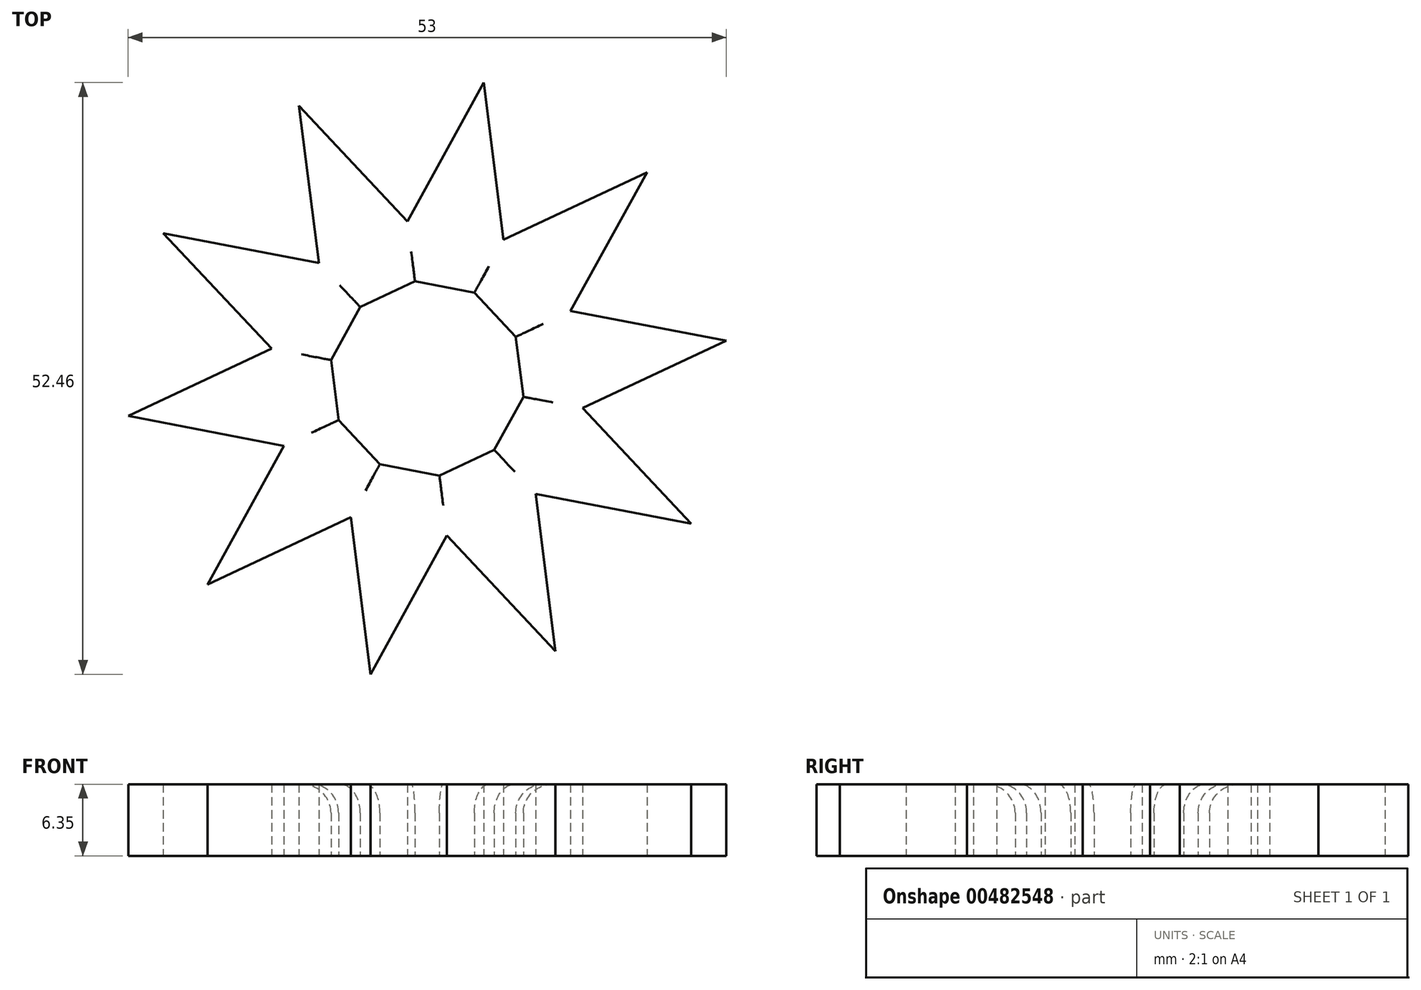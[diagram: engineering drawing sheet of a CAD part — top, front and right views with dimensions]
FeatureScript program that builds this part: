
annotation { "Feature Type Name" : "Feature", "Feature Type Description" : "" }
export const myFeature = defineFeature(function(context is Context, id is Id, definition is map)
    precondition{}
    {
        {
            var Q0;
            Q0=qCreatedBy(makeId("Top.planeOp"),FACE);
            var sketch = newSketch(context, id + "F0", { "sketchPlane" : qUnion([Q0])});
            skCircle(sketch, "E0.cCircle", {"center": v(0, 0) * mm, "radius": 25.4 * mm, "construction": true});
            skLineSegment(sketch, "E0.0", {"start": v(-23.4, 12.88) * mm, "end": v(-11.36, 24.17) * mm});
            skLineSegment(sketch, "E0.1", {"start": v(-11.36, 24.17) * mm, "end": v(5.02, 26.23) * mm});
            skLineSegment(sketch, "E0.2", {"start": v(5.02, 26.23) * mm, "end": v(19.48, 18.27) * mm});
            skLineSegment(sketch, "E0.3", {"start": v(19.48, 18.27) * mm, "end": v(26.5, 3.34) * mm});
            skLineSegment(sketch, "E0.4", {"start": v(26.5, 3.34) * mm, "end": v(23.4, -12.88) * mm});
            skLineSegment(sketch, "E0.5", {"start": v(23.4, -12.88) * mm, "end": v(11.36, -24.17) * mm});
            skLineSegment(sketch, "E0.6", {"start": v(11.36, -24.17) * mm, "end": v(-5.02, -26.23) * mm});
            skLineSegment(sketch, "E0.7", {"start": v(-5.02, -26.23) * mm, "end": v(-19.48, -18.27) * mm});
            skLineSegment(sketch, "E0.8", {"start": v(-19.48, -18.27) * mm, "end": v(-26.5, -3.34) * mm});
            skLineSegment(sketch, "E0.9", {"start": v(-26.5, -3.34) * mm, "end": v(-23.4, 12.88) * mm});
            skPoint(sketch, "E0.0.midPoint", {"position": v(-17.38, 18.52) * mm});
            skLineSegment(sketch, "E1", {"start": v(-19.48, -18.27) * mm, "end": v(5.02, 26.23) * mm});
            skLineSegment(sketch, "E2", {"start": v(5.02, 26.23) * mm, "end": v(11.36, -24.17) * mm});
            skLineSegment(sketch, "E3", {"start": v(11.36, -24.17) * mm, "end": v(-23.4, 12.88) * mm});
            skLineSegment(sketch, "E4", {"start": v(-23.4, 12.88) * mm, "end": v(26.5, 3.34) * mm});
            skLineSegment(sketch, "E5", {"start": v(26.5, 3.34) * mm, "end": v(-19.48, -18.27) * mm});
            skLineSegment(sketch, "E6", {"start": v(-26.5, -3.34) * mm, "end": v(19.48, 18.27) * mm});
            skLineSegment(sketch, "E7", {"start": v(19.48, 18.27) * mm, "end": v(-5.02, -26.23) * mm});
            skLineSegment(sketch, "E8", {"start": v(-5.02, -26.23) * mm, "end": v(-11.36, 24.17) * mm});
            skLineSegment(sketch, "E9", {"start": v(-11.36, 24.17) * mm, "end": v(23.4, -12.88) * mm});
            skLineSegment(sketch, "E10", {"start": v(23.4, -12.88) * mm, "end": v(-26.5, -3.34) * mm});
            skSolve(sketch);
        }
        {
            var Q0;
            {var subQ1=sQuery(id+"F0.wireOp",EDGE,"E3");var subQ3=sQuery(id+"F0.wireOp",EDGE,"E6");var subQ4=makeQuery(id+"F0.imprint","INTERSECT",VERTEX,{"derivedFrom":[subQ1,subQ3]});Q0=makeQuery(id+"F0.imprint","IMPRINT",FACE,{"disambiguationData":[TD([[makeQuery(id+"F0.imprint","IMPRINT",EDGE,{"disambiguationData":[TD([[subQ4,-1.0]])],"derivedFrom":subQ3}),1.0]])]});}
            var Q1;
            {var subQ0=sQuery(id+"F0.wireOp",EDGE,"E3");var subQ1=sQuery(id+"F0.wireOp",EDGE,"E1");var subQ2=makeQuery(id+"F0.imprint","INTERSECT",VERTEX,{"derivedFrom":[subQ1,subQ0]});Q1=makeQuery(id+"F0.imprint","IMPRINT",FACE,{"disambiguationData":[TD([[makeQuery(id+"F0.imprint","IMPRINT",EDGE,{"disambiguationData":[TD([[subQ2,-1.0]])],"derivedFrom":subQ1}),1.0]])]});}
            var Q2;
            {var subQ0=sQuery(id+"F0.wireOp",EDGE,"E10");var subQ1=sQuery(id+"F0.wireOp",EDGE,"E1");var subQ2=makeQuery(id+"F0.imprint","INTERSECT",VERTEX,{"derivedFrom":[subQ1,subQ0]});Q2=makeQuery(id+"F0.imprint","IMPRINT",FACE,{"disambiguationData":[TD([[makeQuery(id+"F0.imprint","IMPRINT",EDGE,{"disambiguationData":[TD([[subQ2,-1.0]])],"derivedFrom":subQ1}),1.0]])]});}
            var Q3;
            {var subQ0=sQuery(id+"F0.wireOp",EDGE,"E5");var subQ5=sQuery(id+"F0.wireOp",EDGE,"E8");var subQ6=makeQuery(id+"F0.imprint","INTERSECT",VERTEX,{"derivedFrom":[subQ0,subQ5]});Q3=makeQuery(id+"F0.imprint","IMPRINT",FACE,{"disambiguationData":[TD([[makeQuery(id+"F0.imprint","IMPRINT",EDGE,{"disambiguationData":[TD([[subQ6,-1.0]])],"derivedFrom":subQ5}),1.0]])]});}
            var Q4;
            {var subQ0=sQuery(id+"F0.wireOp",EDGE,"E7");var subQ1=sQuery(id+"F0.wireOp",EDGE,"E3");var subQ2=makeQuery(id+"F0.imprint","INTERSECT",VERTEX,{"derivedFrom":[subQ1,subQ0]});Q4=makeQuery(id+"F0.imprint","IMPRINT",FACE,{"disambiguationData":[TD([[makeQuery(id+"F0.imprint","IMPRINT",EDGE,{"disambiguationData":[TD([[subQ2,-1.0]])],"derivedFrom":subQ1}),1.0]])]});}
            var Q5;
            {var subQ0=sQuery(id+"F0.wireOp",EDGE,"E3");var subQ5=sQuery(id+"F0.wireOp",EDGE,"E7");var subQ6=makeQuery(id+"F0.imprint","INTERSECT",VERTEX,{"derivedFrom":[subQ0,subQ5]});Q5=makeQuery(id+"F0.imprint","IMPRINT",FACE,{"disambiguationData":[TD([[makeQuery(id+"F0.imprint","IMPRINT",EDGE,{"disambiguationData":[TD([[subQ6,1.0]])],"derivedFrom":subQ5}),1.0]])]});}
            var Q6;
            {var subQ0=sQuery(id+"F0.wireOp",EDGE,"E5");var subQ1=sQuery(id+"F0.wireOp",EDGE,"E2");var subQ2=makeQuery(id+"F0.imprint","INTERSECT",VERTEX,{"derivedFrom":[subQ1,subQ0]});Q6=makeQuery(id+"F0.imprint","IMPRINT",FACE,{"disambiguationData":[TD([[makeQuery(id+"F0.imprint","IMPRINT",EDGE,{"disambiguationData":[TD([[subQ2,-1.0]])],"derivedFrom":subQ1}),1.0]])]});}
            var Q7;
            {var subQ1=sQuery(id+"F0.wireOp",EDGE,"E4");var subQ3=sQuery(id+"F0.wireOp",EDGE,"E7");var subQ4=makeQuery(id+"F0.imprint","INTERSECT",VERTEX,{"derivedFrom":[subQ1,subQ3]});Q7=makeQuery(id+"F0.imprint","IMPRINT",FACE,{"disambiguationData":[TD([[makeQuery(id+"F0.imprint","IMPRINT",EDGE,{"disambiguationData":[TD([[subQ4,-1.0]])],"derivedFrom":subQ3}),1.0]])]});}
            var Q8;
            {var subQ0=sQuery(id+"F0.wireOp",EDGE,"E6");var subQ1=sQuery(id+"F0.wireOp",EDGE,"E2");var subQ2=makeQuery(id+"F0.imprint","INTERSECT",VERTEX,{"derivedFrom":[subQ1,subQ0]});Q8=makeQuery(id+"F0.imprint","IMPRINT",FACE,{"disambiguationData":[TD([[makeQuery(id+"F0.imprint","IMPRINT",EDGE,{"disambiguationData":[TD([[subQ2,-1.0]])],"derivedFrom":subQ1}),1.0]])]});}
            var Q9;
            {var subQ0=sQuery(id+"F0.wireOp",EDGE,"E2");var subQ5=sQuery(id+"F0.wireOp",EDGE,"E6");var subQ6=makeQuery(id+"F0.imprint","INTERSECT",VERTEX,{"derivedFrom":[subQ0,subQ5]});Q9=makeQuery(id+"F0.imprint","IMPRINT",FACE,{"disambiguationData":[TD([[makeQuery(id+"F0.imprint","IMPRINT",EDGE,{"disambiguationData":[TD([[subQ6,1.0]])],"derivedFrom":subQ5}),1.0]])]});}
            var Q10;
            {var subQ0=sQuery(id+"F0.wireOp",EDGE,"E4");var subQ1=sQuery(id+"F0.wireOp",EDGE,"E1");var subQ2=makeQuery(id+"F0.imprint","INTERSECT",VERTEX,{"derivedFrom":[subQ1,subQ0]});Q10=makeQuery(id+"F0.imprint","IMPRINT",FACE,{"disambiguationData":[TD([[makeQuery(id+"F0.imprint","IMPRINT",EDGE,{"disambiguationData":[TD([[subQ2,-1.0]])],"derivedFrom":subQ1}),1.0]])]});}
            var Q11;
            {var subQ0=sQuery(id+"F0.wireOp",EDGE,"E6");var subQ1=sQuery(id+"F0.wireOp",EDGE,"E1");var subQ2=makeQuery(id+"F0.imprint","INTERSECT",VERTEX,{"derivedFrom":[subQ1,subQ0]});Q11=makeQuery(id+"F0.imprint","IMPRINT",FACE,{"disambiguationData":[TD([[makeQuery(id+"F0.imprint","IMPRINT",EDGE,{"disambiguationData":[TD([[subQ2,-1.0]])],"derivedFrom":subQ1}),1.0]])]});}
            var Q12;
            {var subQ0=sQuery(id+"F0.wireOp",EDGE,"E4");var subQ1=sQuery(id+"F0.wireOp",EDGE,"E1");var subQ2=makeQuery(id+"F0.imprint","INTERSECT",VERTEX,{"derivedFrom":[subQ1,subQ0]});Q12=makeQuery(id+"F0.imprint","IMPRINT",FACE,{"disambiguationData":[TD([[makeQuery(id+"F0.imprint","IMPRINT",EDGE,{"disambiguationData":[TD([[subQ2,-1.0]])],"derivedFrom":subQ1}),-1.0]])]});}
            var Q13;
            {var subQ0=sQuery(id+"F0.wireOp",EDGE,"E6");var subQ1=sQuery(id+"F0.wireOp",EDGE,"E2");var subQ2=makeQuery(id+"F0.imprint","INTERSECT",VERTEX,{"derivedFrom":[subQ1,subQ0]});Q13=makeQuery(id+"F0.imprint","IMPRINT",FACE,{"disambiguationData":[TD([[makeQuery(id+"F0.imprint","IMPRINT",EDGE,{"disambiguationData":[TD([[subQ2,-1.0]])],"derivedFrom":subQ1}),-1.0]])]});}
            var Q14;
            {var subQ0=sQuery(id+"F0.wireOp",EDGE,"E4");var subQ1=sQuery(id+"F0.wireOp",EDGE,"E2");var subQ2=makeQuery(id+"F0.imprint","INTERSECT",VERTEX,{"derivedFrom":[subQ1,subQ0]});Q14=makeQuery(id+"F0.imprint","IMPRINT",FACE,{"disambiguationData":[TD([[makeQuery(id+"F0.imprint","IMPRINT",EDGE,{"disambiguationData":[TD([[subQ2,-1.0]])],"derivedFrom":subQ1}),1.0]])]});}
            var Q15;
            {var subQ0=sQuery(id+"F0.wireOp",EDGE,"E5");var subQ1=sQuery(id+"F0.wireOp",EDGE,"E2");var subQ2=makeQuery(id+"F0.imprint","INTERSECT",VERTEX,{"derivedFrom":[subQ1,subQ0]});Q15=makeQuery(id+"F0.imprint","IMPRINT",FACE,{"disambiguationData":[TD([[makeQuery(id+"F0.imprint","IMPRINT",EDGE,{"disambiguationData":[TD([[subQ2,-1.0]])],"derivedFrom":subQ1}),-1.0]])]});}
            var Q16;
            {var subQ0=sQuery(id+"F0.wireOp",EDGE,"E7");var subQ1=sQuery(id+"F0.wireOp",EDGE,"E3");var subQ2=makeQuery(id+"F0.imprint","INTERSECT",VERTEX,{"derivedFrom":[subQ1,subQ0]});Q16=makeQuery(id+"F0.imprint","IMPRINT",FACE,{"disambiguationData":[TD([[makeQuery(id+"F0.imprint","IMPRINT",EDGE,{"disambiguationData":[TD([[subQ2,-1.0]])],"derivedFrom":subQ1}),-1.0]])]});}
            var Q17;
            {var subQ0=sQuery(id+"F0.wireOp",EDGE,"E5");var subQ1=sQuery(id+"F0.wireOp",EDGE,"E3");var subQ2=makeQuery(id+"F0.imprint","INTERSECT",VERTEX,{"derivedFrom":[subQ1,subQ0]});Q17=makeQuery(id+"F0.imprint","IMPRINT",FACE,{"disambiguationData":[TD([[makeQuery(id+"F0.imprint","IMPRINT",EDGE,{"disambiguationData":[TD([[subQ2,-1.0]])],"derivedFrom":subQ1}),1.0]])]});}
            var Q18;
            {var subQ0=sQuery(id+"F0.wireOp",EDGE,"E10");var subQ1=sQuery(id+"F0.wireOp",EDGE,"E1");var subQ2=makeQuery(id+"F0.imprint","INTERSECT",VERTEX,{"derivedFrom":[subQ1,subQ0]});Q18=makeQuery(id+"F0.imprint","IMPRINT",FACE,{"disambiguationData":[TD([[makeQuery(id+"F0.imprint","IMPRINT",EDGE,{"disambiguationData":[TD([[subQ2,-1.0]])],"derivedFrom":subQ1}),-1.0]])]});}
            var Q19;
            {var subQ0=sQuery(id+"F0.wireOp",EDGE,"E5");var subQ1=sQuery(id+"F0.wireOp",EDGE,"E3");var subQ2=makeQuery(id+"F0.imprint","INTERSECT",VERTEX,{"derivedFrom":[subQ1,subQ0]});Q19=makeQuery(id+"F0.imprint","IMPRINT",FACE,{"disambiguationData":[TD([[makeQuery(id+"F0.imprint","IMPRINT",EDGE,{"disambiguationData":[TD([[subQ2,-1.0]])],"derivedFrom":subQ1}),-1.0]])]});}
            var Q20;
            {var subQ0=sQuery(id+"F0.wireOp",EDGE,"E7");var subQ1=sQuery(id+"F0.wireOp",EDGE,"E5");var subQ2=makeQuery(id+"F0.imprint","INTERSECT",VERTEX,{"derivedFrom":[subQ1,subQ0]});Q20=makeQuery(id+"F0.imprint","IMPRINT",FACE,{"disambiguationData":[TD([[makeQuery(id+"F0.imprint","IMPRINT",EDGE,{"disambiguationData":[TD([[subQ2,-1.0]])],"derivedFrom":subQ1}),1.0]])]});}
            var Q21;
            {var subQ0=sQuery(id+"F0.wireOp",EDGE,"E7");var subQ1=sQuery(id+"F0.wireOp",EDGE,"E2");var subQ2=makeQuery(id+"F0.imprint","INTERSECT",VERTEX,{"derivedFrom":[subQ1,subQ0]});Q21=makeQuery(id+"F0.imprint","IMPRINT",FACE,{"disambiguationData":[TD([[makeQuery(id+"F0.imprint","IMPRINT",EDGE,{"disambiguationData":[TD([[subQ2,-1.0]])],"derivedFrom":subQ1}),-1.0]])]});}
            var Q22;
            {var subQ0=sQuery(id+"F0.wireOp",EDGE,"E4");var subQ1=sQuery(id+"F0.wireOp",EDGE,"E2");var subQ2=makeQuery(id+"F0.imprint","INTERSECT",VERTEX,{"derivedFrom":[subQ1,subQ0]});Q22=makeQuery(id+"F0.imprint","IMPRINT",FACE,{"disambiguationData":[TD([[makeQuery(id+"F0.imprint","IMPRINT",EDGE,{"disambiguationData":[TD([[subQ2,-1.0]])],"derivedFrom":subQ1}),-1.0]])]});}
            var Q23;
            {var subQ0=sQuery(id+"F0.wireOp",EDGE,"E7");var subQ1=sQuery(id+"F0.wireOp",EDGE,"E2");var subQ2=makeQuery(id+"F0.imprint","INTERSECT",VERTEX,{"derivedFrom":[subQ1,subQ0]});Q23=makeQuery(id+"F0.imprint","IMPRINT",FACE,{"disambiguationData":[TD([[makeQuery(id+"F0.imprint","IMPRINT",EDGE,{"disambiguationData":[TD([[subQ2,-1.0]])],"derivedFrom":subQ1}),1.0]])]});}
            var Q24;
            {var subQ0=sQuery(id+"F0.wireOp",EDGE,"E9");var subQ1=sQuery(id+"F0.wireOp",EDGE,"E2");var subQ2=makeQuery(id+"F0.imprint","INTERSECT",VERTEX,{"derivedFrom":[subQ1,subQ0]});Q24=makeQuery(id+"F0.imprint","IMPRINT",FACE,{"disambiguationData":[TD([[makeQuery(id+"F0.imprint","IMPRINT",EDGE,{"disambiguationData":[TD([[subQ2,-1.0]])],"derivedFrom":subQ1}),1.0]])]});}
            var Q25;
            {var subQ0=sQuery(id+"F0.wireOp",EDGE,"E6");var subQ1=sQuery(id+"F0.wireOp",EDGE,"E4");var subQ2=makeQuery(id+"F0.imprint","INTERSECT",VERTEX,{"derivedFrom":[subQ1,subQ0]});Q25=makeQuery(id+"F0.imprint","IMPRINT",FACE,{"disambiguationData":[TD([[makeQuery(id+"F0.imprint","IMPRINT",EDGE,{"disambiguationData":[TD([[subQ2,-1.0]])],"derivedFrom":subQ1}),1.0]])]});}
            var Q26;
            {var subQ0=sQuery(id+"F0.wireOp",EDGE,"E6");var subQ1=sQuery(id+"F0.wireOp",EDGE,"E1");var subQ2=makeQuery(id+"F0.imprint","INTERSECT",VERTEX,{"derivedFrom":[subQ1,subQ0]});Q26=makeQuery(id+"F0.imprint","IMPRINT",FACE,{"disambiguationData":[TD([[makeQuery(id+"F0.imprint","IMPRINT",EDGE,{"disambiguationData":[TD([[subQ2,-1.0]])],"derivedFrom":subQ1}),-1.0]])]});}
            var Q27;
            {var subQ0=sQuery(id+"F0.wireOp",EDGE,"E3");var subQ1=sQuery(id+"F0.wireOp",EDGE,"E1");var subQ2=makeQuery(id+"F0.imprint","INTERSECT",VERTEX,{"derivedFrom":[subQ1,subQ0]});Q27=makeQuery(id+"F0.imprint","IMPRINT",FACE,{"disambiguationData":[TD([[makeQuery(id+"F0.imprint","IMPRINT",EDGE,{"disambiguationData":[TD([[subQ2,-1.0]])],"derivedFrom":subQ1}),-1.0]])]});}
            var Q28;
            {var subQ0=sQuery(id+"F0.wireOp",EDGE,"E10");var subQ1=sQuery(id+"F0.wireOp",EDGE,"E3");var subQ2=makeQuery(id+"F0.imprint","INTERSECT",VERTEX,{"derivedFrom":[subQ1,subQ0]});Q28=makeQuery(id+"F0.imprint","IMPRINT",FACE,{"disambiguationData":[TD([[makeQuery(id+"F0.imprint","IMPRINT",EDGE,{"disambiguationData":[TD([[subQ2,-1.0]])],"derivedFrom":subQ1}),1.0]])]});}
            var Q29;
            {var subQ0=sQuery(id+"F0.wireOp",EDGE,"E8");var subQ1=sQuery(id+"F0.wireOp",EDGE,"E1");var subQ2=makeQuery(id+"F0.imprint","INTERSECT",VERTEX,{"derivedFrom":[subQ1,subQ0]});Q29=makeQuery(id+"F0.imprint","IMPRINT",FACE,{"disambiguationData":[TD([[makeQuery(id+"F0.imprint","IMPRINT",EDGE,{"disambiguationData":[TD([[subQ2,-1.0]])],"derivedFrom":subQ1}),1.0]])]});}
            extrude(context, id + "F1", {"entities" : qUnion([Q0, Q1, Q2, Q3, Q4, Q5, Q6, Q7, Q8, Q9, Q10, Q11, Q12, Q13, Q14, Q15, Q16, Q17, Q18, Q19, Q20, Q21, Q22, Q23, Q24, Q25, Q26, Q27, Q28, Q29]), "depth" : 6.35 * mm});
        }
        {
            var Q0;
            {var subQ0=sQuery(id+"F0.wireOp",EDGE,"E9");Q0=makeQuery(id+"F1.opExtrude","CAP_EDGE",EDGE,{"disambiguationData":[OSD([subQ0]),TDD([makeQuery(id+"F0.imprint","IMPRINT",EDGE,{"disambiguationData":[TD([[makeQuery(id+"F0.imprint","INTERSECT",VERTEX,{"derivedFrom":[sQuery(id+"F0.wireOp",EDGE,"E2"),subQ0]}),1.0]])],"derivedFrom":subQ0})])],"isStart":false});}
            var Q1;
            {var subQ0=sQuery(id+"F0.wireOp",EDGE,"E2");Q1=makeQuery(id+"F1.opExtrude","CAP_EDGE",EDGE,{"disambiguationData":[OSD([subQ0]),TDD([makeQuery(id+"F0.imprint","IMPRINT",EDGE,{"disambiguationData":[TD([[makeQuery(id+"F0.imprint","INTERSECT",VERTEX,{"derivedFrom":[subQ0,sQuery(id+"F0.wireOp",EDGE,"E9")]}),-1.0]])],"derivedFrom":subQ0})])],"isStart":false});}
            var Q2;
            {var subQ0=sQuery(id+"F0.wireOp",EDGE,"E10");Q2=makeQuery(id+"F1.opExtrude","CAP_EDGE",EDGE,{"disambiguationData":[OSD([subQ0]),TDD([makeQuery(id+"F0.imprint","IMPRINT",EDGE,{"disambiguationData":[TD([[makeQuery(id+"F0.imprint","INTERSECT",VERTEX,{"derivedFrom":[sQuery(id+"F0.wireOp",EDGE,"E3"),subQ0]}),1.0]])],"derivedFrom":subQ0})])],"isStart":false});}
            var Q3;
            {var subQ0=sQuery(id+"F0.wireOp",EDGE,"E3");Q3=makeQuery(id+"F1.opExtrude","CAP_EDGE",EDGE,{"disambiguationData":[OSD([subQ0]),TDD([makeQuery(id+"F0.imprint","IMPRINT",EDGE,{"disambiguationData":[TD([[makeQuery(id+"F0.imprint","INTERSECT",VERTEX,{"derivedFrom":[subQ0,sQuery(id+"F0.wireOp",EDGE,"E10")]}),-1.0]])],"derivedFrom":subQ0})])],"isStart":false});}
            var Q4;
            {var subQ0=sQuery(id+"F0.wireOp",EDGE,"E8");Q4=makeQuery(id+"F1.opExtrude","CAP_EDGE",EDGE,{"disambiguationData":[OSD([subQ0]),TDD([makeQuery(id+"F0.imprint","IMPRINT",EDGE,{"disambiguationData":[TD([[makeQuery(id+"F0.imprint","INTERSECT",VERTEX,{"derivedFrom":[sQuery(id+"F0.wireOp",EDGE,"E1"),subQ0]}),1.0]])],"derivedFrom":subQ0})])],"isStart":false});}
            var Q5;
            {var subQ0=sQuery(id+"F0.wireOp",EDGE,"E6");Q5=makeQuery(id+"F1.opExtrude","CAP_EDGE",EDGE,{"disambiguationData":[OSD([subQ0]),TDD([makeQuery(id+"F0.imprint","IMPRINT",EDGE,{"disambiguationData":[TD([[makeQuery(id+"F0.imprint","INTERSECT",VERTEX,{"derivedFrom":[sQuery(id+"F0.wireOp",EDGE,"E1"),subQ0]}),-1.0]])],"derivedFrom":subQ0})])],"isStart":false});}
            var Q6;
            {var subQ0=sQuery(id+"F0.wireOp",EDGE,"E4");Q6=makeQuery(id+"F1.opExtrude","CAP_EDGE",EDGE,{"disambiguationData":[OSD([subQ0]),TDD([makeQuery(id+"F0.imprint","IMPRINT",EDGE,{"disambiguationData":[TD([[makeQuery(id+"F0.imprint","INTERSECT",VERTEX,{"derivedFrom":[subQ0,sQuery(id+"F0.wireOp",EDGE,"E6")]}),-1.0]])],"derivedFrom":subQ0})])],"isStart":false});}
            var Q7;
            {var subQ0=sQuery(id+"F0.wireOp",EDGE,"E5");Q7=makeQuery(id+"F1.opExtrude","CAP_EDGE",EDGE,{"disambiguationData":[OSD([subQ0]),TDD([makeQuery(id+"F0.imprint","IMPRINT",EDGE,{"disambiguationData":[TD([[makeQuery(id+"F0.imprint","INTERSECT",VERTEX,{"derivedFrom":[subQ0,sQuery(id+"F0.wireOp",EDGE,"E7")]}),-1.0]])],"derivedFrom":subQ0})])],"isStart":false});}
            var Q8;
            {var subQ0=sQuery(id+"F0.wireOp",EDGE,"E7");Q8=makeQuery(id+"F1.opExtrude","CAP_EDGE",EDGE,{"disambiguationData":[OSD([subQ0]),TDD([makeQuery(id+"F0.imprint","IMPRINT",EDGE,{"disambiguationData":[TD([[makeQuery(id+"F0.imprint","INTERSECT",VERTEX,{"derivedFrom":[sQuery(id+"F0.wireOp",EDGE,"E2"),subQ0]}),-1.0]])],"derivedFrom":subQ0})])],"isStart":false});}
            var Q9;
            {var subQ0=sQuery(id+"F0.wireOp",EDGE,"E1");Q9=makeQuery(id+"F1.opExtrude","CAP_EDGE",EDGE,{"disambiguationData":[OSD([subQ0]),TDD([makeQuery(id+"F0.imprint","IMPRINT",EDGE,{"disambiguationData":[TD([[makeQuery(id+"F0.imprint","INTERSECT",VERTEX,{"derivedFrom":[subQ0,sQuery(id+"F0.wireOp",EDGE,"E8")]}),-1.0]])],"derivedFrom":subQ0})])],"isStart":false});}
            fillet(context, id + "F2", {"entities" : qUnion([Q0, Q1, Q2, Q3, Q4, Q5, Q6, Q7, Q8, Q9]), "radius" : 2.54 * mm, "tangentPropagation" : true, "allowEdgeOverflow" : false});
        }
    });
